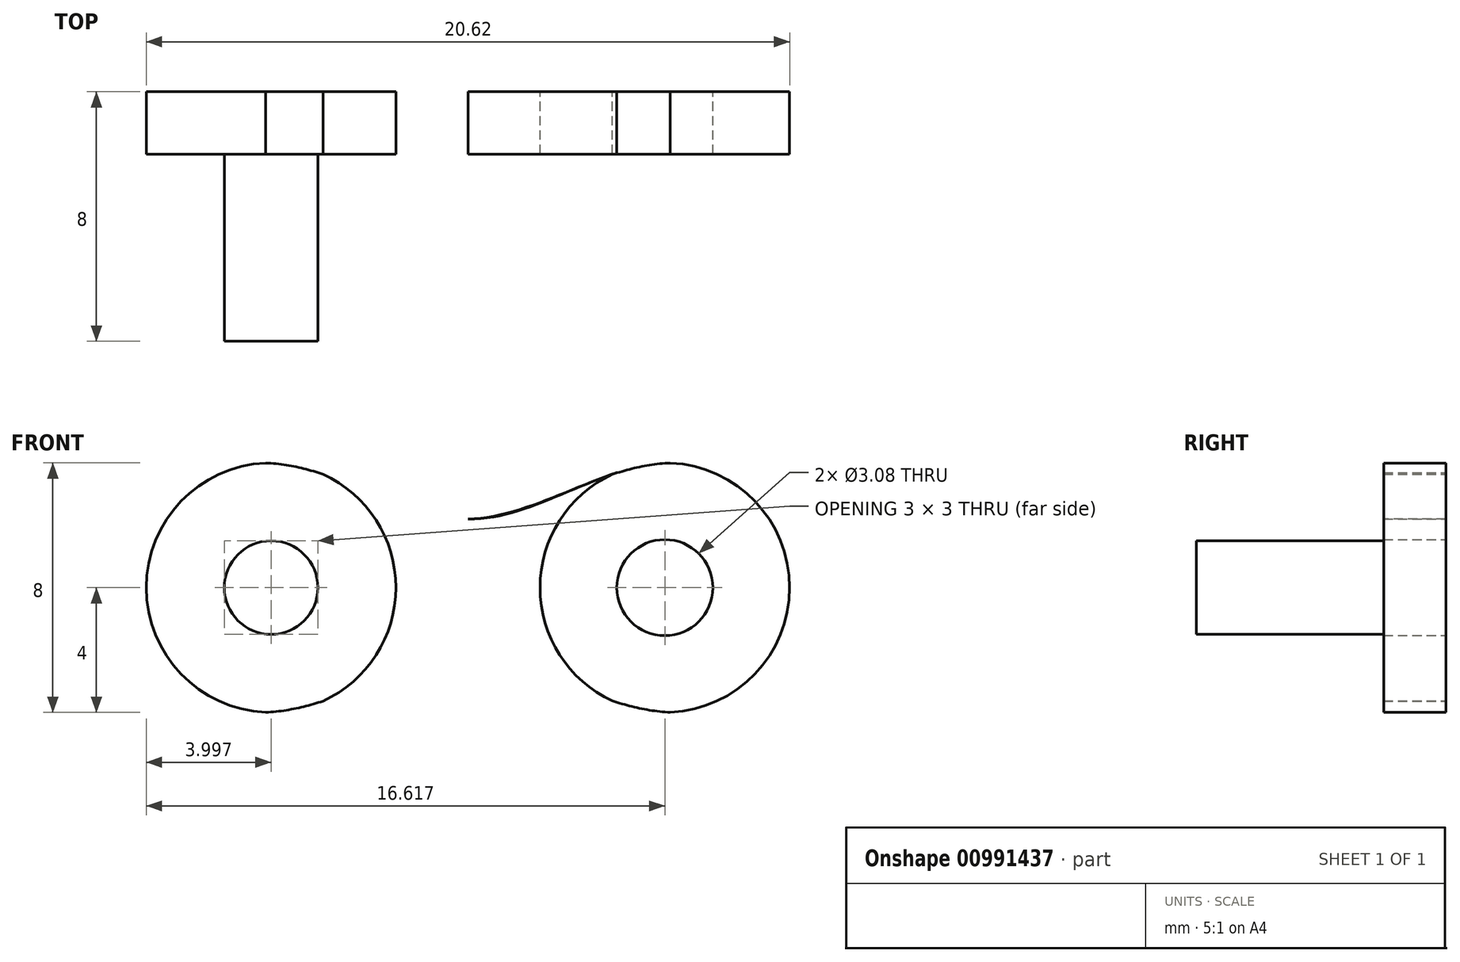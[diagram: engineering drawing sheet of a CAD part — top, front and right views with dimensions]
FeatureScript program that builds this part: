
annotation { "Feature Type Name" : "Feature", "Feature Type Description" : "" }
export const myFeature = defineFeature(function(context is Context, id is Id, definition is map)
    precondition{}
    {
        {
            var Q0;
            Q0=qCreatedBy(makeId("Front.planeOp"),FACE);
            var sketch = newSketch(context, id + "F0", { "sketchPlane" : qUnion([Q0])});
            skCircle(sketch, "E0", {"center": v(-6.31, 0) * mm, "radius": 1.5 * mm});
            skCircle(sketch, "E1", {"center": v(6.3, 0) * mm, "radius": 1.54 * mm});
            skCircle(sketch, "E2", {"center": v(6.3, 0) * mm, "radius": 4 * mm});
            skCircle(sketch, "E3", {"center": v(-6.31, 0) * mm, "radius": 4 * mm});
            skFitSpline(sketch, "E4", {"points": [v(-6.49, 4) * mm, v(0, 2.2) * mm, v(6.3, 4) * mm], "startDerivative": vector(14.5, -0.58) * mm, "endDerivative": vector(10.86, 0.01) * mm});
            skFitSpline(sketch, "E5.MirrorCS", {"points": [v(6.49, 4) * mm, v(0, 2.2) * mm, v(-6.3, 4) * mm], "startDerivative": vector(-14.5, -0.58) * mm, "endDerivative": vector(-10.86, 0.01) * mm});
            skFitSpline(sketch, "E6.MirrorCS", {"points": [v(-6.49, -4) * mm, v(0, -2.2) * mm, v(6.3, -4) * mm], "startDerivative": vector(14.5, 0.58) * mm, "endDerivative": vector(10.86, -0.01) * mm});
            skFitSpline(sketch, "E7.MirrorCS", {"points": [v(6.49, -4) * mm, v(0, -2.2) * mm, v(-6.3, -4) * mm], "startDerivative": vector(-14.5, 0.58) * mm, "endDerivative": vector(-10.86, -0.01) * mm});
            skLineSegment(sketch, "E8", {"start": v(-6.31, 0) * mm, "end": v(-4.81, 0) * mm});
            skSolve(sketch);
        }
        {
            var Q0;
            Q0=makeQuery(id+"F0.imprint","IMPRINT",FACE,{"disambiguationData":[TD([[makeQuery(id+"F0.imprint","IMPRINT",EDGE,{"derivedFrom":sQuery(id+"F0.wireOp",EDGE,"E0")}),-1.0]])]});
            var Q1;
            {var subQ1=sQuery(id+"F0.wireOp",EDGE,"E4");var subQ5=sQuery(id+"F0.wireOp",EDGE,"E2");var subQ6=makeQuery(id+"F0.imprint","INTERSECT",VERTEX,{"disambiguationData":[OD(1.0)],"derivedFrom":[subQ5,subQ1]});Q1=makeQuery(id+"F0.imprint","IMPRINT",FACE,{"disambiguationData":[TD([[makeQuery(id+"F0.imprint","IMPRINT",EDGE,{"disambiguationData":[TD([[subQ6,-1.0]])],"derivedFrom":subQ5}),-1.0]])]});}
            var Q2;
            Q2=makeQuery(id+"F0.imprint","IMPRINT",FACE,{"disambiguationData":[TD([[makeQuery(id+"F0.imprint","IMPRINT",EDGE,{"derivedFrom":sQuery(id+"F0.wireOp",EDGE,"E1")}),-1.0]])]});
            extrude(context, id + "F1", {"entities" : qUnion([Q0, Q1, Q2]), "depth" : 2 * mm, "offsetDistance" : 25.4 * mm});
        }
        {
            var Q0;
            Q0=sQuery(id+"F0.wireOp",EDGE,"E8");
            extrude(context, id + "F2", {"bodyType" : ExtendedToolBodyType.SURFACE, "surfaceEntities" : qUnion([Q0]), "depth" : 8 * mm, "offsetDistance" : 25.4 * mm});
        }
        {
            var Q0;
            Q0=makeQuery(id+"F2.opExtrude","SWEPT_FACE",FACE,{"disambiguationData":[OSD([sQuery(id+"F0.wireOp",EDGE,"E8")])]});
            var Q1;
            Q1=makeQuery(id+"F2.opExtrude","SWEPT_EDGE",EDGE,{"disambiguationData":[OSD([sQuery(id+"F0.wireOp",VERTEX,"E8.start")])]});
            revolve(context, id + "F3", {"operationType" : NewBodyOperationType.ADD, "surfaceOperationType" : NewSurfaceOperationType.NEW, "entities" : qUnion([Q0]), "axis" : qUnion([Q1]), "revolveType" : RevolveType.FULL});
        }
        {
            var Q0;
            Q0=makeQuery(id+"F1.opExtrude","SWEPT_BODY",BODY,{"disambiguationData":[OSD([sQuery(id+"F0.wireOp",EDGE,"E0"),sQuery(id+"F0.wireOp",EDGE,"E1"),sQuery(id+"F0.wireOp",EDGE,"E2"),sQuery(id+"F0.wireOp",EDGE,"E3"),sQuery(id+"F0.wireOp",EDGE,"E4"),sQuery(id+"F0.wireOp",EDGE,"E5.MirrorCS"),sQuery(id+"F0.wireOp",EDGE,"E6.MirrorCS"),sQuery(id+"F0.wireOp",EDGE,"E7.MirrorCS")])]});
            transform(context, id + "F4", {"entities" : qUnion([Q0]), "transformType" : TransformType.TRANSLATION_3D, "dx" : 0 * mm, "dy" : 0 * mm, "dz" : 0 * mm, "makeCopy" : true});
        }
    });
